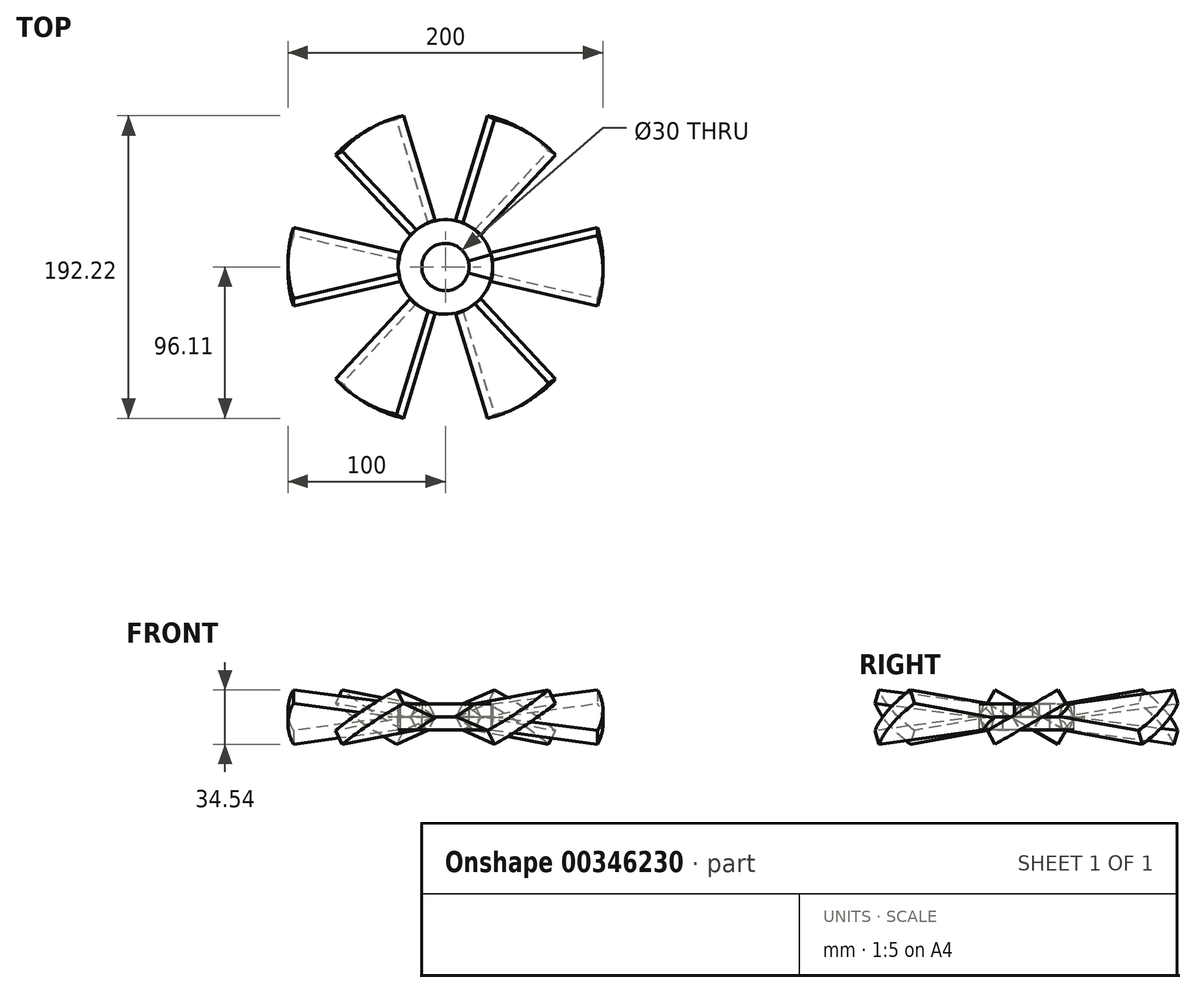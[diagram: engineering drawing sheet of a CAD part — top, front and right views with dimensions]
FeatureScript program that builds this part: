
annotation { "Feature Type Name" : "Feature", "Feature Type Description" : "" }
export const myFeature = defineFeature(function(context is Context, id is Id, definition is map)
    precondition{}
    {
        {
            var Q0;
            Q0=qCreatedBy(makeId("Top.planeOp"),FACE);
            var sketch = newSketch(context, id + "F0", { "sketchPlane" : qUnion([Q0])});
            skCircle(sketch, "E0", {"center": v(0, 0) * mm, "radius": 15 * mm});
            skCircle(sketch, "E1", {"center": v(0, 0) * mm, "radius": 100 * mm});
            skCircle(sketch, "E2", {"center": v(0, 0) * mm, "radius": 30 * mm});
            skLineSegment(sketch, "E3", {"start": v(0, 0) * mm, "end": v(100, 0) * mm});
            skLineSegment(sketch, "E4", {"start": v(0, 0) * mm, "end": v(96.6, 25.88) * mm});
            skLineSegment(sketch, "E5.MirrorCS", {"start": v(0, 0) * mm, "end": v(96.6, -25.88) * mm});
            skSolve(sketch);
        }
        {
            var Q0;
            {var subQ0=sQuery(id+"F0.wireOp",EDGE,"E3");var subQ1=sQuery(id+"F0.wireOp",EDGE,"E1");var subQ2=makeQuery(id+"F0.imprint","INTERSECT",VERTEX,{"derivedFrom":[subQ1,subQ0]});Q0=makeQuery(id+"F0.imprint","IMPRINT",FACE,{"disambiguationData":[TD([[makeQuery(id+"F0.imprint","IMPRINT",EDGE,{"disambiguationData":[TD([[subQ2,-1.0]])],"derivedFrom":subQ1}),1.0]])]});}
            var Q1;
            {var subQ0=sQuery(id+"F0.wireOp",EDGE,"E3");var subQ1=sQuery(id+"F0.wireOp",EDGE,"E1");var subQ2=makeQuery(id+"F0.imprint","INTERSECT",VERTEX,{"derivedFrom":[subQ1,subQ0]});Q1=makeQuery(id+"F0.imprint","IMPRINT",FACE,{"disambiguationData":[TD([[makeQuery(id+"F0.imprint","IMPRINT",EDGE,{"disambiguationData":[TD([[subQ2,1.0]])],"derivedFrom":subQ1}),1.0]])]});}
            extrude(context, id + "F1", {"entities" : qUnion([Q0, Q1]), "depth" : 5 * mm, "hasSecondDirection" : true, "secondDirectionOppositeDirection" : true, "secondDirectionDepth" : 5 * mm});
        }
        {
            var Q0;
            Q0=makeQuery(id+"F1.opExtrude","SWEPT_BODY",BODY,{"disambiguationData":[OSD([sQuery(id+"F0.wireOp",EDGE,"E1"),sQuery(id+"F0.wireOp",EDGE,"E2"),sQuery(id+"F0.wireOp",EDGE,"E4"),sQuery(id+"F0.wireOp",EDGE,"E5.MirrorCS")])]});
            var Q1;
            Q1=sQuery(id+"F0.wireOp",EDGE,"E3");
            transform(context, id + "F2", {"entities" : qUnion([Q0]), "transformType" : TransformType.ROTATION, "transformAxis" : qUnion([Q1]), "angle" : 30 * degree, "makeCopy" : false});
        }
        {
            var Q0;
            Q0=qCreatedBy(makeId("Front.planeOp"),FACE);
            var sketch = newSketch(context, id + "F3", { "sketchPlane" : qUnion([Q0])});
            skLineSegment(sketch, "E6", {"start": v(0, 0) * mm, "end": v(0, 55) * mm});
            skSolve(sketch);
        }
        {
            var Q0;
            Q0=makeQuery(id+"F1.opExtrude","SWEPT_BODY",BODY,{"disambiguationData":[OSD([sQuery(id+"F0.wireOp",EDGE,"E1"),sQuery(id+"F0.wireOp",EDGE,"E2"),sQuery(id+"F0.wireOp",EDGE,"E4"),sQuery(id+"F0.wireOp",EDGE,"E5.MirrorCS")])]});
            var Q1;
            Q1=sQuery(id+"F3.wireOp",EDGE,"E6");
            circularPattern(context, id + "F4", {"entities" : qUnion([Q0]), "axis" : qUnion([Q1]), "angle" : 360 * degree, "instanceCount" : 6, "equalSpace" : true});
        }
        {
            var Q0;
            {var subQ0=sQuery(id+"F0.wireOp",EDGE,"E4");var subQ1=sQuery(id+"F0.wireOp",EDGE,"E0");var subQ2=makeQuery(id+"F0.imprint","INTERSECT",VERTEX,{"derivedFrom":[subQ1,subQ0]});Q0=makeQuery(id+"F0.imprint","IMPRINT",FACE,{"disambiguationData":[TD([[makeQuery(id+"F0.imprint","IMPRINT",EDGE,{"disambiguationData":[TD([[subQ2,-1.0]])],"derivedFrom":subQ1}),-1.0]])]});}
            var Q1;
            Q1=makeQuery(id+"F4.opPattern","COPY",VERTEX,{"derivedFrom":makeQuery(id+"F1.opExtrude","CAP_VERTEX",VERTEX,{"disambiguationData":[OSD([sQuery(id+"F0.wireOp",EDGE,"E2"),sQuery(id+"F0.wireOp",EDGE,"E4")])],"isStart":false}),"instanceName":"1"});
            extrude(context, id + "F5", {"entities" : qUnion([Q0]), "endBound" : BoundingType.UP_TO_VERTEX, "endBoundEntityVertex" : qUnion([Q1]), "depth" : 25 * mm});
        }
        {
            var Q0;
            {var subQ0=sQuery(id+"F0.wireOp",EDGE,"E4");var subQ1=sQuery(id+"F0.wireOp",EDGE,"E0");var subQ2=makeQuery(id+"F0.imprint","INTERSECT",VERTEX,{"derivedFrom":[subQ1,subQ0]});Q0=makeQuery(id+"F0.imprint","IMPRINT",FACE,{"disambiguationData":[TD([[makeQuery(id+"F0.imprint","IMPRINT",EDGE,{"disambiguationData":[TD([[subQ2,1.0]])],"derivedFrom":subQ1}),-1.0]])]});}
            var Q1;
            {var subQ0=sQuery(id+"F0.wireOp",EDGE,"E3");var subQ1=sQuery(id+"F0.wireOp",EDGE,"E0");var subQ2=makeQuery(id+"F0.imprint","INTERSECT",VERTEX,{"derivedFrom":[subQ1,subQ0]});Q1=makeQuery(id+"F0.imprint","IMPRINT",FACE,{"disambiguationData":[TD([[makeQuery(id+"F0.imprint","IMPRINT",EDGE,{"disambiguationData":[TD([[subQ2,1.0]])],"derivedFrom":subQ1}),-1.0]])]});}
            var Q2;
            Q2=makeQuery(id+"F5.opExtrude","CAP_VERTEX",VERTEX,{"disambiguationData":[OSD([sQuery(id+"F0.wireOp",EDGE,"E0"),sQuery(id+"F0.wireOp",EDGE,"E4"),dummyQuery(id+"F5.vertexPlane.planeOp",FACE)])],"isStart":false});
            extrude(context, id + "F6", {"entities" : qUnion([Q0, Q1]), "endBound" : BoundingType.UP_TO_VERTEX, "endBoundEntityVertex" : qUnion([Q2]), "depth" : 25 * mm});
        }
        {
            var Q0;
            {var subQ0=sQuery(id+"F0.wireOp",EDGE,"E4");var subQ1=sQuery(id+"F0.wireOp",EDGE,"E0");var subQ2=makeQuery(id+"F0.imprint","INTERSECT",VERTEX,{"derivedFrom":[subQ1,subQ0]});Q0=makeQuery(id+"F0.imprint","IMPRINT",FACE,{"disambiguationData":[TD([[makeQuery(id+"F0.imprint","IMPRINT",EDGE,{"disambiguationData":[TD([[subQ2,-1.0]])],"derivedFrom":subQ1}),-1.0]])]});}
            var Q1;
            {var subQ0=sQuery(id+"F0.wireOp",EDGE,"E3");var subQ1=sQuery(id+"F0.wireOp",EDGE,"E0");var subQ2=makeQuery(id+"F0.imprint","INTERSECT",VERTEX,{"derivedFrom":[subQ1,subQ0]});Q1=makeQuery(id+"F0.imprint","IMPRINT",FACE,{"disambiguationData":[TD([[makeQuery(id+"F0.imprint","IMPRINT",EDGE,{"disambiguationData":[TD([[subQ2,1.0]])],"derivedFrom":subQ1}),-1.0]])]});}
            var Q2;
            {var subQ0=sQuery(id+"F0.wireOp",EDGE,"E4");var subQ1=sQuery(id+"F0.wireOp",EDGE,"E0");var subQ2=makeQuery(id+"F0.imprint","INTERSECT",VERTEX,{"derivedFrom":[subQ1,subQ0]});Q2=makeQuery(id+"F0.imprint","IMPRINT",FACE,{"disambiguationData":[TD([[makeQuery(id+"F0.imprint","IMPRINT",EDGE,{"disambiguationData":[TD([[subQ2,1.0]])],"derivedFrom":subQ1}),-1.0]])]});}
            var Q3;
            Q3=makeQuery(id+"F4.opPattern","COPY",VERTEX,{"derivedFrom":makeQuery(id+"F1.opExtrude","CAP_VERTEX",VERTEX,{"disambiguationData":[OSD([sQuery(id+"F0.wireOp",EDGE,"E2"),sQuery(id+"F0.wireOp",EDGE,"E5.MirrorCS")])],"isStart":true}),"instanceName":"3"});
            extrude(context, id + "F7", {"entities" : qUnion([Q0, Q1, Q2]), "endBound" : BoundingType.UP_TO_VERTEX, "oppositeDirection" : true, "endBoundEntityVertex" : qUnion([Q3]), "depth" : 25 * mm});
        }
    });
